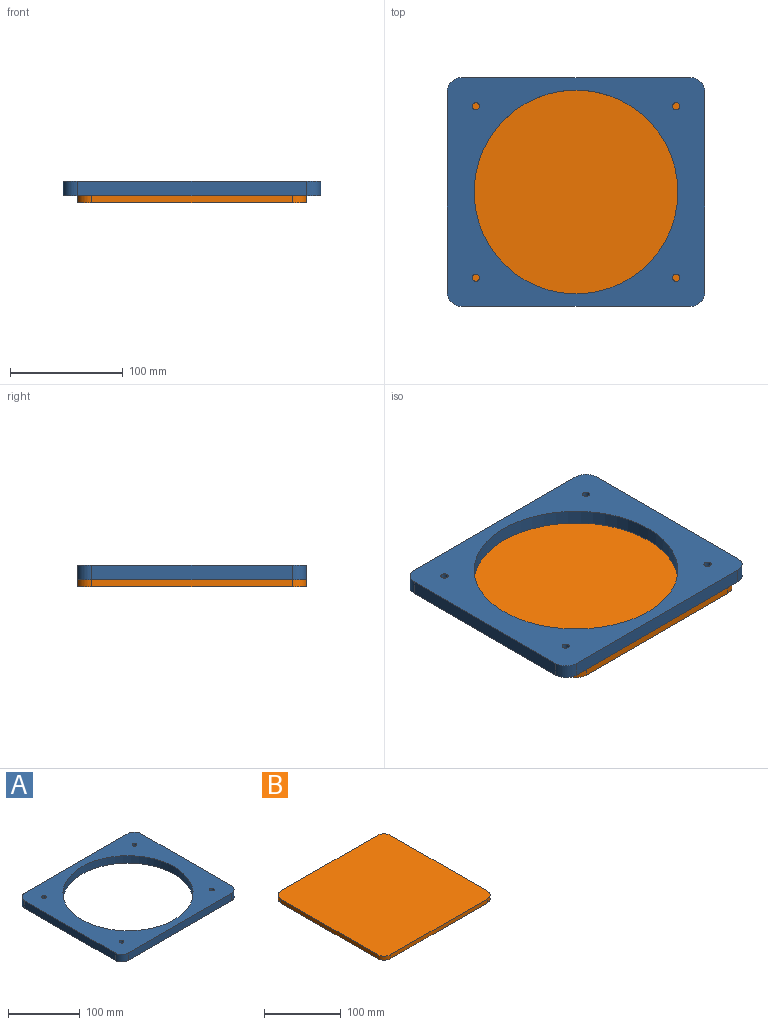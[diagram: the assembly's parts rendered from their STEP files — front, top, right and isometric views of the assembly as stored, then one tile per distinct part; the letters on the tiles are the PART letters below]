
ASSEMBLY  parts=2 mates=1
PART A: 15 faces, bbox 228.6x203.2x12.7 mm
  f0: cylinder r=12.7mm len=12.7mm, axis (0,0,-1), area 253.4mm2, adj f1,f7,f8,f9
  f1: plane 203.2x12.7mm, normal (0,-1,0), area 2580.6mm2, adj f0,f2,f8,f9
  f2: cylinder r=12.7mm len=12.7mm, axis (0,0,-1), area 253.4mm2, adj f1,f3,f8,f9
  f3: plane 177.8x12.7mm, normal (1,0,0), area 2258.1mm2, adj f2,f4,f8,f9
  f4: cylinder r=12.7mm len=12.7mm, axis (0,0,-1), area 253.4mm2, adj f3,f5,f8,f9
  f5: plane 203.2x12.7mm, normal (0,1,0), area 2580.6mm2, adj f4,f6,f8,f9
  f6: cylinder r=12.7mm len=12.7mm, axis (0,0,-1), area 253.4mm2, adj f5,f7,f8,f9
  f7: plane 177.8x12.7mm, normal (-1,0,0), area 2258.1mm2, adj f0,f6,f8,f9
  f8: plane 228.6x203.2mm, normal (0,0,1), area 20463.1mm2, adj f0,f1,f2,f3,f4,f5,f6,f7
  f9: plane 228.6x203.2mm, normal (0,0,-1), area 20463.1mm2, adj f0,f1,f2,f3,f4,f5,f6,f7
  f10: cylinder r=90.49mm len=180.98mm, axis (0,0,1), area 7220.6mm2, adj f8,f9
  f11: cylinder r=3.17mm len=12.7mm, axis (0,0,1), area 253.4mm2, adj f8,f9
  f12: cylinder r=3.17mm len=12.7mm, axis (0,0,1), area 253.4mm2, adj f8,f9
  f13: cylinder r=3.17mm len=12.7mm, axis (0,0,1), area 253.4mm2, adj f8,f9
  f14: cylinder r=3.17mm len=12.7mm, axis (0,0,1), area 253.4mm2, adj f8,f9
PART B: 10 faces, bbox 203.2x203.2x6.4 mm
  f0: cylinder r=12.7mm len=12.7mm, axis (0,0,-1), area 126.7mm2, adj f1,f7,f8,f9
  f1: plane 177.8x6.35mm, normal (0,-1,0), area 1129mm2, adj f0,f2,f8,f9
  f2: cylinder r=12.7mm len=12.7mm, axis (0,0,-1), area 126.7mm2, adj f1,f3,f8,f9
  f3: plane 177.8x6.35mm, normal (1,0,0), area 1129mm2, adj f2,f4,f8,f9
  f4: cylinder r=12.7mm len=12.7mm, axis (0,0,-1), area 126.7mm2, adj f3,f5,f8,f9
  f5: plane 177.8x6.35mm, normal (0,1,0), area 1129mm2, adj f4,f6,f8,f9
  f6: cylinder r=12.7mm len=12.7mm, axis (0,0,-1), area 126.7mm2, adj f5,f7,f8,f9
  f7: plane 177.8x6.35mm, normal (-1,0,0), area 1129mm2, adj f0,f6,f8,f9
  f8: plane 203.2x203.2mm, normal (0,0,1), area 41151.8mm2, adj f0,f1,f2,f3,f4,f5,f6,f7
  f9: plane 203.2x203.2mm, normal (0,0,-1), area 41151.8mm2, adj f0,f1,f2,f3,f4,f5,f6,f7
PLACE A t=(-22.39,-14.1,1.41)mm
PLACE B t=(-22.39,-14.1,-4.94)mm fixed
MATE planar B.f8 <-> A.f10  axis (0,0,1) through (-22.39,-14.1,1.41)mm
